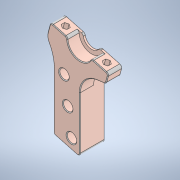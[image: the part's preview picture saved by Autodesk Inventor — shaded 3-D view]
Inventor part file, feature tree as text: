
AUTODESK INVENTOR PART (.ipt)
format: ipt  version: 2021.2 (Build 252289000, 289)  size: 344,576 bytes
history: native  units: mm
features: other x4, fillet x2, chamfer x2
ambient origin geometry x8: Origin, YZ Plane, XZ Plane, XY Plane, X Axis, Y Axis, Z Axis, Center Point
bodies: Body1 (feature_tree)
feature tree (8):
  other  "Твёрдое тело.ipt"
  fillet  "Сопряжение1"  Radius=10.0mm
  fillet  "Сопряжение2"  Radius=2.0mm
  chamfer  "Фаска1"  Distance=2.0mm
  chamfer  "Фаска2"  Distance=2.0mm Angle=45.0deg
  other  "Ножка правая верх::Твёрдое тело.ipt"
  other  "Элемент создания тегов1"
  other  "Твердое тело1"
